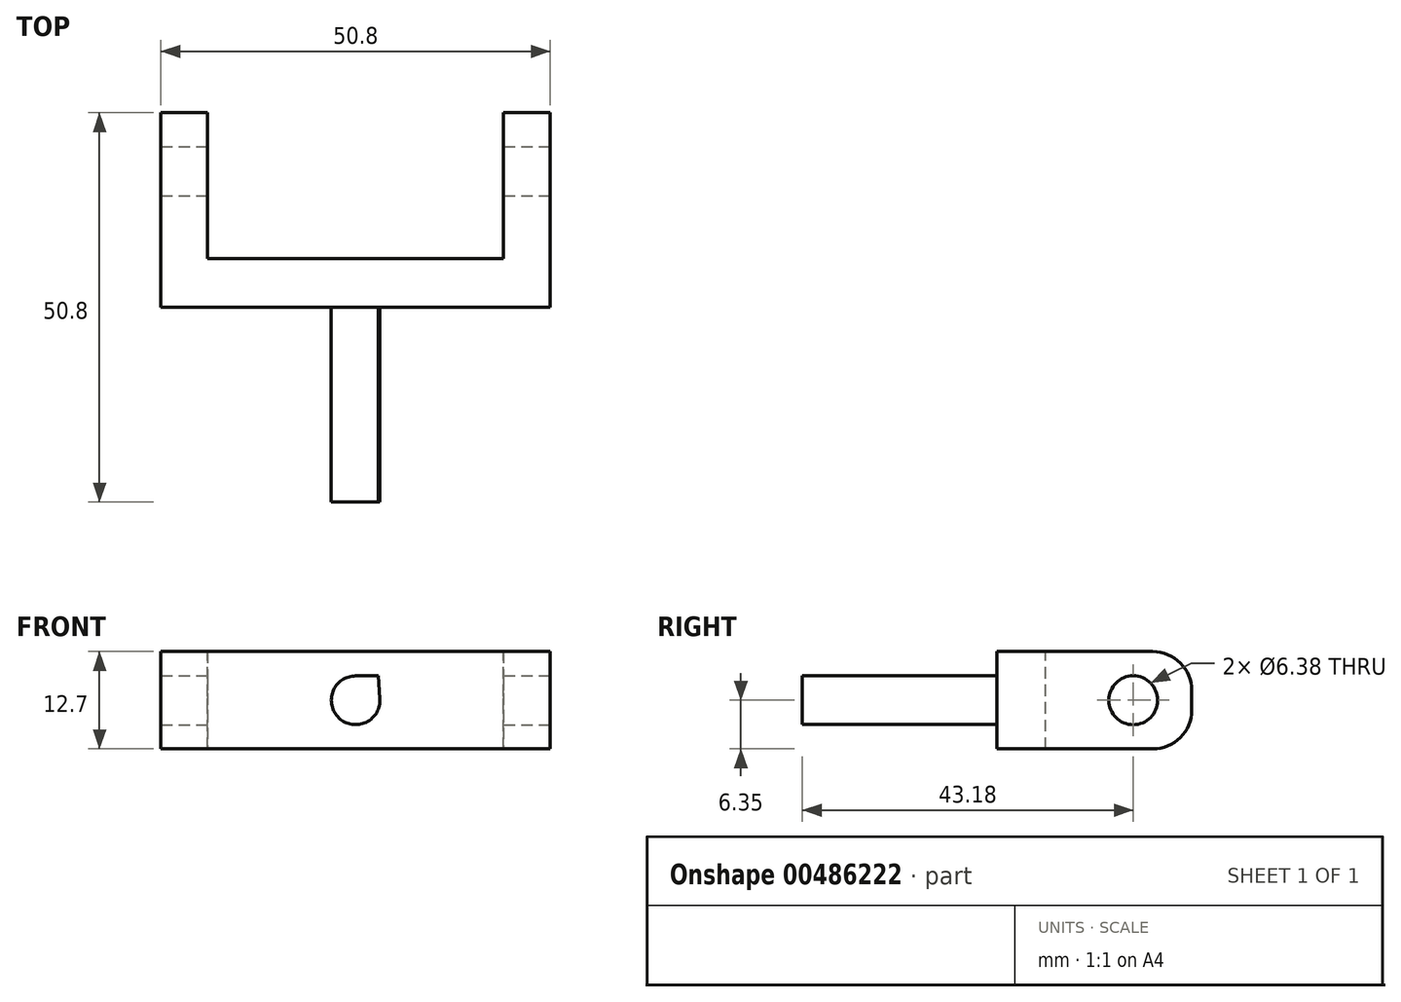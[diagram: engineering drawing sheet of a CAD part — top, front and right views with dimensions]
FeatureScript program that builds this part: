
annotation { "Feature Type Name" : "Feature", "Feature Type Description" : "" }
export const myFeature = defineFeature(function(context is Context, id is Id, definition is map)
    precondition{}
    {
        {
            var Q0;
            Q0=qCreatedBy(makeId("Front.planeOp"),FACE);
            var sketch = newSketch(context, id + "F0", { "sketchPlane" : qUnion([Q0])});
            skLineSegment(sketch, "E0.bottom", {"start": v(0, 0) * mm, "end": v(50.8, 0) * mm});
            skLineSegment(sketch, "E0.top", {"start": v(0, 12.7) * mm, "end": v(50.8, 12.7) * mm});
            skLineSegment(sketch, "E0.left", {"start": v(0, 0) * mm, "end": v(0, 12.7) * mm});
            skLineSegment(sketch, "E0.right", {"start": v(50.8, 0) * mm, "end": v(50.8, 12.7) * mm});
            skSolve(sketch);
        }
        {
            var Q0;
            Q0 = qSketchRegion(id + "F0", true);
            extrude(context, id + "F1", {"entities" : qUnion([Q0]), "depth" : 25.4 * mm, "offsetDistance" : 25.4 * mm});
        }
        {
            var Q0;
            Q0=makeQuery(id+"F1.opExtrude","SWEPT_FACE",FACE,{"disambiguationData":[OSD([sQuery(id+"F0.wireOp",EDGE,"E0.top")])]});
            var sketch = newSketch(context, id + "F2", { "sketchPlane" : qUnion([Q0])});
            skLineSegment(sketch, "E1.bottom", {"start": v(0, -25.4) * mm, "end": v(6.1, -25.4) * mm});
            skLineSegment(sketch, "E1.top", {"start": v(0, 0) * mm, "end": v(6.35, 0) * mm});
            skLineSegment(sketch, "E1.left", {"start": v(0, -25.4) * mm, "end": v(0, 0) * mm});
            skLineSegment(sketch, "E2", {"start": v(25.4, 0) * mm, "end": v(25.4, -25.4) * mm, "construction": true});
            skLineSegment(sketch, "E3.bottom", {"start": v(0, 0) * mm, "end": v(6.1, 0) * mm});
            skLineSegment(sketch, "E3.left", {"start": v(0, 0) * mm, "end": v(0, -25.4) * mm});
            skLineSegment(sketch, "E3.right", {"start": v(6.1, 0) * mm, "end": v(6.1, -25.4) * mm});
            skLineSegment(sketch, "E4", {"start": v(6.1, 0) * mm, "end": v(25.4, 0) * mm, "construction": true});
            skLineSegment(sketch, "E5.MirrorCS", {"start": v(44.7, 0) * mm, "end": v(25.4, 0) * mm, "construction": true});
            skLineSegment(sketch, "E6.MirrorCS", {"start": v(44.7, 0) * mm, "end": v(44.7, -25.4) * mm});
            skLineSegment(sketch, "E7", {"start": v(6.35, 0) * mm, "end": v(44.7, 0) * mm, "construction": true});
            skLineSegment(sketch, "E8", {"start": v(44.7, -25.4) * mm, "end": v(6.1, -25.4) * mm, "construction": true});
            skLineSegment(sketch, "E9", {"start": v(6.1, -25.4) * mm, "end": v(6.1, -19.05) * mm});
            skLineSegment(sketch, "E10", {"start": v(6.1, -19.05) * mm, "end": v(44.7, -19.05) * mm});
            skSolve(sketch);
        }
        {
            var Q0;
            {var subQ0=sQuery(id+"F2.wireOp",EDGE,"E10");Q0=makeQuery(id+"F2.imprint","IMPRINT",FACE,{"disambiguationData":[TD([[makeQuery(id+"F2.imprint","IMPRINT",EDGE,{"derivedFrom":subQ0}),1.0]])]});}
            extrude(context, id + "F3", {"entities" : qUnion([Q0]), "operationType" : NewBodyOperationType.REMOVE, "oppositeDirection" : true, "depth" : 25.4 * mm, "offsetDistance" : 25.4 * mm});
        }
        {
            var Q0;
            Q0=makeQuery(id+"F1.opExtrude","CAP_FACE",FACE,{"disambiguationData":[OSD([sQuery(id+"F0.wireOp",EDGE,"E0.bottom"),sQuery(id+"F0.wireOp",EDGE,"E0.top"),sQuery(id+"F0.wireOp",EDGE,"E0.left"),sQuery(id+"F0.wireOp",EDGE,"E0.right")])],"isStart":false});
            var sketch = newSketch(context, id + "F4", { "sketchPlane" : qUnion([Q0])});
            skLineSegment(sketch, "E11", {"start": v(25.4, 12.7) * mm, "end": v(25.4, 0) * mm, "construction": true});
            skLineSegment(sketch, "E12", {"start": v(25.4, 0) * mm, "end": v(0, 6.35) * mm, "construction": true});
            skLineSegment(sketch, "E13", {"start": v(0, 6.35) * mm, "end": v(50.8, 6.35) * mm, "construction": true});
            skCircle(sketch, "E14", {"center": v(25.4, 6.35) * mm, "radius": 3.18 * mm});
            skLineSegment(sketch, "E15", {"start": v(25.4, 9.52) * mm, "end": v(28.36, 9.52) * mm});
            skLineSegment(sketch, "E16", {"start": v(28.36, 9.52) * mm, "end": v(28.58, 6.35) * mm});
            skSolve(sketch);
        }
        {
            var Q0;
            Q0 = qSketchRegion(id + "F4", true);
            extrude(context, id + "F5", {"entities" : qUnion([Q0]), "operationType" : NewBodyOperationType.ADD, "depth" : 25.4 * mm, "offsetDistance" : 25.4 * mm});
        }
        {
            var Q0;
            Q0 = qSketchRegion(id + "F4", true);
            extrude(context, id + "F6", {"entities" : qUnion([Q0]), "depth" : 25.4 * mm, "offsetDistance" : 25.4 * mm});
        }
        {
            var Q0;
            Q0=makeQuery(id+"F1.opExtrude","SWEPT_FACE",FACE,{"disambiguationData":[OSD([sQuery(id+"F0.wireOp",EDGE,"E0.right")])]});
            var sketch = newSketch(context, id + "F7", { "sketchPlane" : qUnion([Q0])});
            skLineSegment(sketch, "E17", {"start": v(0, 6.35) * mm, "end": v(-7.62, 6.35) * mm, "construction": true});
            skLineSegment(sketch, "E18", {"start": v(-7.62, 6.35) * mm, "end": v(-7.62, 12.7) * mm, "construction": true});
            skLineSegment(sketch, "E19", {"start": v(-7.62, 12.7) * mm, "end": v(-7.62, 0) * mm, "construction": true});
            skCircle(sketch, "E20", {"center": v(-7.62, 6.35) * mm, "radius": 3.19 * mm});
            skPoint(sketch, "E20.perimeterSnap0", {"position": v(-3.81, 6.35) * mm});
            skPoint(sketch, "E20.perimeterSnap1", {"position": v(-7.62, 9.52) * mm});
            skSolve(sketch);
        }
        {
            var Q0;
            Q0 = qSketchRegion(id + "F7", true);
            extrude(context, id + "F8", {"entities" : qUnion([Q0]), "operationType" : NewBodyOperationType.REMOVE, "oppositeDirection" : true, "depth" : 76.2 * mm, "offsetDistance" : 25.4 * mm});
        }
        {
            var Q0;
            {var subQ0=sQuery(id+"F0.wireOp",EDGE,"E0.right");var subQ1=sQuery(id+"F0.wireOp",EDGE,"E0.top");Q0=makeQuery(id+"F3.boolean.opBoolean","SPLIT",EDGE,{"disambiguationData":[TD([makeQuery(id+"F1.opExtrude","SWEPT_FACE",FACE,{"disambiguationData":[OSD([subQ0])]})])],"derivedFrom":makeQuery(id+"F1.opExtrude","CAP_EDGE",EDGE,{"disambiguationData":[OSD([subQ1])],"isStart":true})});}
            var Q1;
            {var subQ0=sQuery(id+"F0.wireOp",EDGE,"E0.bottom");var subQ1=sQuery(id+"F0.wireOp",EDGE,"E0.right");Q1=makeQuery(id+"F3.boolean.opBoolean","SPLIT",EDGE,{"disambiguationData":[TD([makeQuery(id+"F1.opExtrude","SWEPT_FACE",FACE,{"disambiguationData":[OSD([subQ1])]})])],"derivedFrom":makeQuery(id+"F1.opExtrude","CAP_EDGE",EDGE,{"disambiguationData":[OSD([subQ0])],"isStart":true})});}
            var Q2;
            {var subQ0=sQuery(id+"F0.wireOp",EDGE,"E0.left");var subQ1=sQuery(id+"F0.wireOp",EDGE,"E0.top");Q2=makeQuery(id+"F3.boolean.opBoolean","SPLIT",EDGE,{"disambiguationData":[TD([makeQuery(id+"F1.opExtrude","SWEPT_FACE",FACE,{"disambiguationData":[OSD([subQ0])]})])],"derivedFrom":makeQuery(id+"F1.opExtrude","CAP_EDGE",EDGE,{"disambiguationData":[OSD([subQ1])],"isStart":true})});}
            var Q3;
            {var subQ0=sQuery(id+"F0.wireOp",EDGE,"E0.bottom");var subQ1=sQuery(id+"F0.wireOp",EDGE,"E0.left");Q3=makeQuery(id+"F3.boolean.opBoolean","SPLIT",EDGE,{"disambiguationData":[TD([makeQuery(id+"F1.opExtrude","SWEPT_FACE",FACE,{"disambiguationData":[OSD([subQ1])]})])],"derivedFrom":makeQuery(id+"F1.opExtrude","CAP_EDGE",EDGE,{"disambiguationData":[OSD([subQ0])],"isStart":true})});}
            fillet(context, id + "F9", {"entities" : qUnion([Q0, Q1, Q2, Q3]), "tangentPropagation" : true, "radius" : 5.08 * mm, "defaultsChanged" : false, "vertexSettings" : [], "allowEdgeOverflow" : false});
        }
    });
